# Revit family: 237805 STIEBEL ELTRON LWZ 130
name_source: partatom
category: HLS-Bauteile
units: mm (PartAtom-declared; Revit-internal decimal feet)

## family parameters
Arbeitsebenenbasiert = Nein
Beim Laden mit Abzugskörper schneiden = Nein
Bemaßung runder Anschluss = Durchmesser verwenden
Gemeinsam genutzt = Ja
Immer vertikal = Ja
OmniClass-Nummer = 23.75.00.00
OmniClass-Titel = Climate Control (HVAC)
Raumberechnungspunkt = Nein
Teiletyp = Normal

## types (1)
- Standard
    Hersteller = Stiebel Eltron
    Installation Space = Ja
    LIN_ARTICLE_NUMBER = 237805
    LIN_LONG_DESCRIPTION = STIEBEL ELTRON Zentrales Lüftungsgerät
LWZ 130, Deckengerät mit WRG
Anwendung  Das zentrale Lüftungsgerät
mit Wärmerückgewinnung eignet zur Be-
und Entlüftung von Wohnungen und kleinen
Einfamilienhäusern. Komfortmerkmale
Kompaktes Design, optimiert für den
Einbau in eine abgehängte Decke,
empfohlen für Wohnflächen bis ca. 130
m2.  Der kabelgebundene Regler mit
Multifunktions-Display eignet sich auch
als Bedieneinheit für die Wandmontage
und verfügt über einen integrierten
Feuchtesensor und ein Wochenprogramm.
Das Gerät verfügt über folgende
Ausstattungsdetails: Effiziente
Konstant-Volumenstrom-Lüfter,
hocheffizienter
Kreuz-Gegenstrom-Wärmeübertrager mit
Feuchterückgewinnung, elektrische
Vorheizung über
Hochleistungsheizregister,
elektronischer Bypass.  Einfacher
Filterwechsel, mit Grobstaubfilter in
der Abluft und Mittelstaubfilter in der
Zuluft, optional können hier auch
Feinstaubfilter eingesetzt
werden.Effizienz  Der
Konstant-Volumenstrom-Lüfter ermöglicht
einen ausbalancierten Luftvolumen-Strom,
was zu einer effizienten Betriebsweise
führt.Installation  Das Deckengerät
wird in Wohneinheiten installiert, die
Luftanschlüsse sind an der rechten und
linken Seite des Gerätes. Das
Elektro-Anschlussfeld lässt sich einfach
erreichen, ohne das Gerät öffnen zu
müssen.  Das EPS-Gehäuse besitzt eine
partielle Blechverkleidung aus
verzinktem Stahlblech.  Der raumseitige
Abschluss erfolgt durch eine bauseitig
zu installierende Serviceklappe.
    LIN_MANUFACTURER = STIEBEL ELTRON GmbH & Co. KG
    LIN_MANUFACTURER_URL = http://www.stiebel-eltron.de
    LIN_PRODUCT_URL = http://erps.stiebel-eltron.de
    LIN_SHORT_DESCRIPTION = STIEBEL ELTRON Zentrales Lüftungsgerät - 
LWZ 130, Deckengerät mit WRG
    Modell = 237805
    Operating Space = Ja

## geometry (parser evidence)
native form markers: Blend x4, Sweep x2
no freeform markers — native parametric forms only
